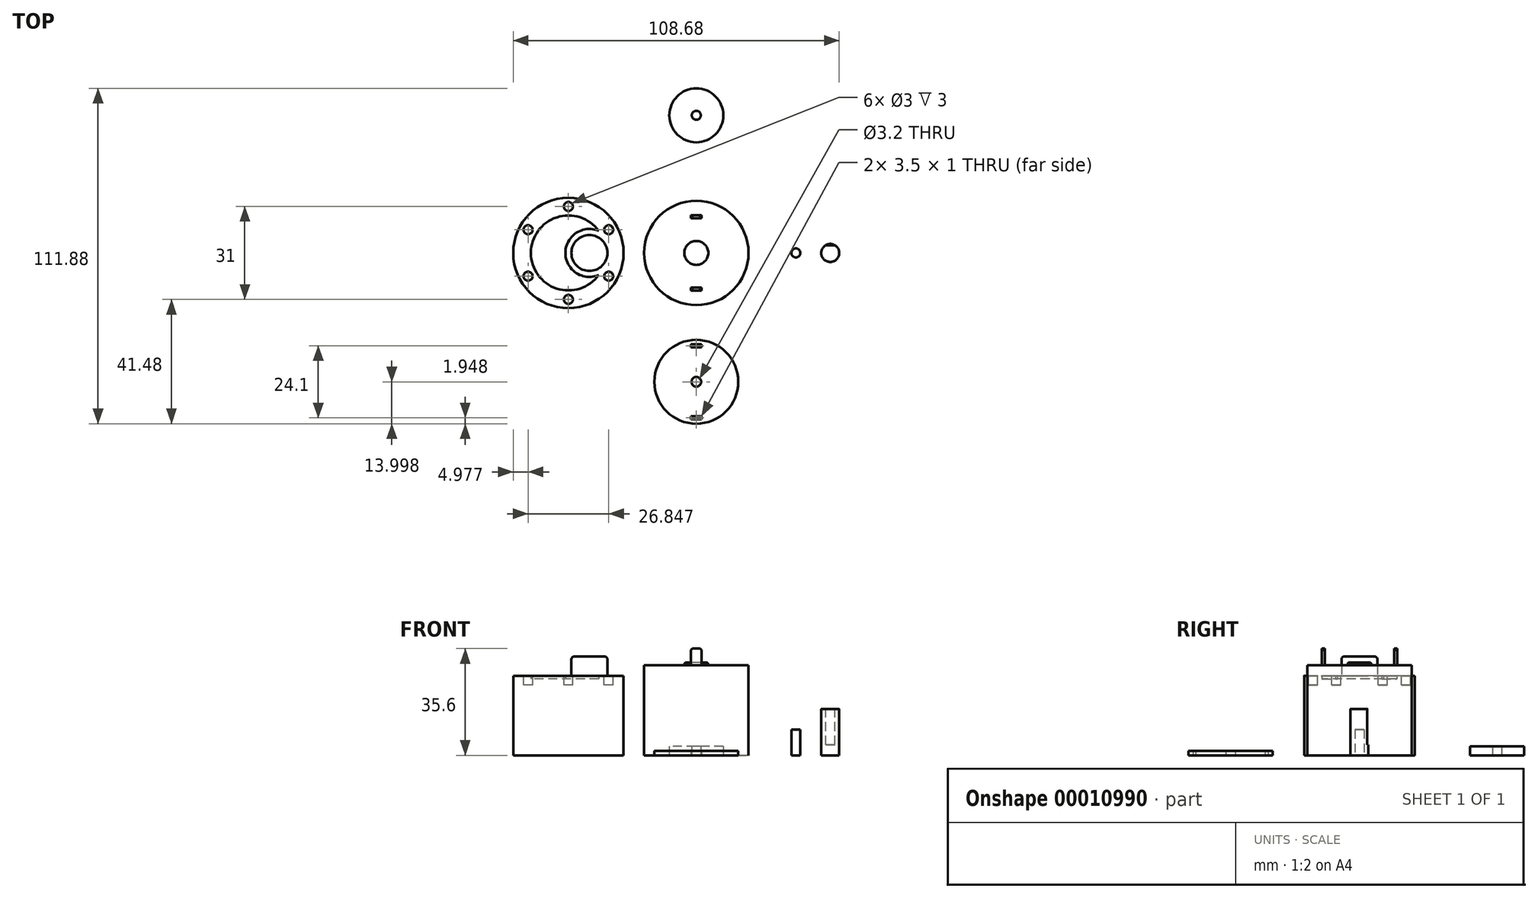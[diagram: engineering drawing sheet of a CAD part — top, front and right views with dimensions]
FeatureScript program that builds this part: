
annotation { "Feature Type Name" : "Feature", "Feature Type Description" : "" }
export const myFeature = defineFeature(function(context is Context, id is Id, definition is map)
    precondition{}
    {
        {
            var Q0;
            Q0=qCreatedBy(makeId("Top.planeOp"),FACE);
            var sketch = newSketch(context, id + "F0", { "sketchPlane" : qUnion([Q0])});
            skCircle(sketch, "E0", {"center": v(-42.64, 0) * mm, "radius": 18.4 * mm});
            skSolve(sketch);
        }
        {
            var Q0;
            Q0=makeQuery(id+"F0.imprint","IMPRINT",FACE,{"disambiguationData":[TD([[makeQuery(id+"F0.imprint","IMPRINT",EDGE,{"derivedFrom":sQuery(id+"F0.wireOp",EDGE,"E0")}),1.0]])]});
            extrude(context, id + "F1", {"entities" : qUnion([Q0]), "depth" : 25.5 * mm});
        }
        {
            var Q0;
            Q0=makeQuery(id+"F1.opExtrude","CAP_FACE",FACE,{"disambiguationData":[OSD([sQuery(id+"F0.wireOp",EDGE,"E0")])],"isStart":false});
            var sketch = newSketch(context, id + "F2", { "sketchPlane" : qUnion([Q0])});
            skArc(sketch, "E1", {"start": v(-32.55, 7.38) * mm, "mid": v(-55.14, 0) * mm, "end": v(-32.55, -7.38) * mm});
            skArc(sketch, "E2", {"start": v(-32.55, 7.38) * mm, "mid": v(-43.64, 0) * mm, "end": v(-32.55, -7.38) * mm});
            skSolve(sketch);
        }
        {
            var Q0;
            Q0=makeQuery(id+"F2.imprint","IMPRINT",FACE,{"disambiguationData":[TD([[makeQuery(id+"F2.imprint","IMPRINT",EDGE,{"derivedFrom":sQuery(id+"F2.wireOp",EDGE,"E1")}),-1.0]])]});
            extrude(context, id + "F3", {"entities" : qUnion([Q0]), "operationType" : NewBodyOperationType.ADD, "depth" : 1 * mm});
        }
        {
            var Q0;
            Q0=makeQuery(id+"F3.opExtrude","CAP_FACE",FACE,{"disambiguationData":[OSD([sQuery(id+"F0.wireOp",EDGE,"E0"),sQuery(id+"F2.wireOp",EDGE,"E1"),sQuery(id+"F2.wireOp",EDGE,"E2")])],"isStart":false});
            var sketch = newSketch(context, id + "F4", { "sketchPlane" : qUnion([Q0])});
            skCircle(sketch, "E3", {"center": v(-35.64, 0) * mm, "radius": 6 * mm});
            skSolve(sketch);
        }
        {
            var Q0;
            Q0=makeQuery(id+"F4.imprint","IMPRINT",FACE,{"disambiguationData":[TD([[makeQuery(id+"F4.imprint","IMPRINT",EDGE,{"derivedFrom":sQuery(id+"F4.wireOp",EDGE,"E3")}),1.0]])]});
            extrude(context, id + "F5", {"entities" : qUnion([Q0]), "operationType" : NewBodyOperationType.ADD, "depth" : 6.5 * mm});
        }
        {
            var Q0;
            Q0=makeQuery(id+"F5.opExtrude","CAP_EDGE",EDGE,{"disambiguationData":[OSD([sQuery(id+"F4.wireOp",EDGE,"E3")])],"isStart":false});
            fillet(context, id + "F6", {"entities" : qUnion([Q0]), "radius" : 1 * mm, "tangentPropagation" : true, "allowEdgeOverflow" : false});
        }
        {
            var Q0;
            Q0=makeQuery(id+"F3.opExtrude","CAP_FACE",FACE,{"disambiguationData":[OSD([sQuery(id+"F0.wireOp",EDGE,"E0"),sQuery(id+"F2.wireOp",EDGE,"E1"),sQuery(id+"F2.wireOp",EDGE,"E2")])],"isStart":false});
            var sketch = newSketch(context, id + "F7", { "sketchPlane" : qUnion([Q0])});
            skCircle(sketch, "E4", {"center": v(-42.64, 15.5) * mm, "radius": 1.5 * mm});
            skCircle(sketch, "E5.1.0", {"center": v(-56.06, 7.75) * mm, "radius": 1.5 * mm});
            skCircle(sketch, "E5.2.0", {"center": v(-56.06, -7.75) * mm, "radius": 1.5 * mm});
            skCircle(sketch, "E5.3.0", {"center": v(-42.64, -15.5) * mm, "radius": 1.5 * mm});
            skCircle(sketch, "E5.4.0", {"center": v(-29.22, -7.75) * mm, "radius": 1.5 * mm});
            skCircle(sketch, "E5.5.0", {"center": v(-29.22, 7.75) * mm, "radius": 1.5 * mm});
            skPoint(sketch, "E5.center", {"position": v(-42.64, 0) * mm});
            skSolve(sketch);
        }
        {
            var Q0;
            Q0 = qSketchRegion(id + "F7", true);
            extrude(context, id + "F8", {"entities" : qUnion([Q0]), "operationType" : NewBodyOperationType.REMOVE, "oppositeDirection" : true, "depth" : 3 * mm});
        }
        {
            var Q0;
            Q0=qCreatedBy(makeId("Top.planeOp"),FACE);
            var sketch = newSketch(context, id + "F9", { "sketchPlane" : qUnion([Q0])});
            skCircle(sketch, "E6", {"center": v(0, 0) * mm, "radius": 17.4 * mm});
            skSolve(sketch);
        }
        {
            var Q0;
            Q0=makeQuery(id+"F9.imprint","IMPRINT",FACE,{"disambiguationData":[TD([[makeQuery(id+"F9.imprint","IMPRINT",EDGE,{"derivedFrom":sQuery(id+"F9.wireOp",EDGE,"E6")}),1.0]])]});
            extrude(context, id + "F10", {"entities" : qUnion([Q0]), "depth" : 30 * mm});
        }
        {
            var Q0;
            Q0=makeQuery(id+"F10.opExtrude","CAP_FACE",FACE,{"disambiguationData":[OSD([sQuery(id+"F9.wireOp",EDGE,"E6")])],"isStart":false});
            var sketch = newSketch(context, id + "F11", { "sketchPlane" : qUnion([Q0])});
            skCircle(sketch, "E7", {"center": v(0, 0) * mm, "radius": 4 * mm});
            skSolve(sketch);
        }
        {
            var Q0;
            Q0=makeQuery(id+"F11.imprint","IMPRINT",FACE,{"disambiguationData":[TD([[makeQuery(id+"F11.imprint","IMPRINT",EDGE,{"derivedFrom":sQuery(id+"F11.wireOp",EDGE,"E7")}),1.0]])]});
            extrude(context, id + "F12", {"entities" : qUnion([Q0]), "operationType" : NewBodyOperationType.ADD, "depth" : 1 * mm});
        }
        {
            var Q0;
            Q0=makeQuery(id+"F12.opExtrude","CAP_EDGE",EDGE,{"disambiguationData":[OSD([sQuery(id+"F11.wireOp",EDGE,"E7")])],"isStart":false});
            fillet(context, id + "F13", {"entities" : qUnion([Q0]), "radius" : 0.7 * mm, "tangentPropagation" : true, "allowEdgeOverflow" : false});
        }
        {
            var Q0;
            Q0=makeQuery(id+"F10.opExtrude","CAP_FACE",FACE,{"disambiguationData":[OSD([sQuery(id+"F9.wireOp",EDGE,"E6")])],"isStart":false});
            var sketch = newSketch(context, id + "F14", { "sketchPlane" : qUnion([Q0])});
            skLineSegment(sketch, "E8.rect.bottom", {"start": v(1.75, 12.55) * mm, "end": v(-1.75, 12.55) * mm});
            skLineSegment(sketch, "E8.rect.top", {"start": v(1.75, 11.55) * mm, "end": v(-1.75, 11.55) * mm});
            skLineSegment(sketch, "E8.rect.left", {"start": v(1.75, 12.55) * mm, "end": v(1.75, 11.55) * mm});
            skLineSegment(sketch, "E8.rect.right", {"start": v(-1.75, 12.55) * mm, "end": v(-1.75, 11.55) * mm});
            skPoint(sketch, "E8.rect.middle", {"position": v(0, 12.05) * mm});
            skLineSegment(sketch, "E9.rect.bottom", {"start": v(1.75, -11.55) * mm, "end": v(-1.75, -11.55) * mm});
            skLineSegment(sketch, "E9.rect.top", {"start": v(1.75, -12.55) * mm, "end": v(-1.75, -12.55) * mm});
            skLineSegment(sketch, "E9.rect.left", {"start": v(1.75, -11.55) * mm, "end": v(1.75, -12.55) * mm});
            skLineSegment(sketch, "E9.rect.right", {"start": v(-1.75, -11.55) * mm, "end": v(-1.75, -12.55) * mm});
            skPoint(sketch, "E9.rect.middle", {"position": v(0, -12.05) * mm});
            skSolve(sketch);
        }
        {
            var Q0;
            Q0 = qSketchRegion(id + "F14", true);
            extrude(context, id + "F15", {"entities" : qUnion([Q0]), "operationType" : NewBodyOperationType.ADD, "depth" : 5.6 * mm});
        }
        {
            var Q0;
            Q0=makeQuery(id+"F15.opExtrude","CAP_EDGE",EDGE,{"disambiguationData":[OSD([sQuery(id+"F14.wireOp",EDGE,"E8.rect.left")])],"isStart":false});
            var Q1;
            Q1=makeQuery(id+"F15.opExtrude","CAP_EDGE",EDGE,{"disambiguationData":[OSD([sQuery(id+"F14.wireOp",EDGE,"E8.rect.right")])],"isStart":false});
            var Q2;
            Q2=makeQuery(id+"F15.opExtrude","CAP_EDGE",EDGE,{"disambiguationData":[OSD([sQuery(id+"F14.wireOp",EDGE,"E9.rect.left")])],"isStart":false});
            var Q3;
            Q3=makeQuery(id+"F15.opExtrude","CAP_EDGE",EDGE,{"disambiguationData":[OSD([sQuery(id+"F14.wireOp",EDGE,"E9.rect.right")])],"isStart":false});
            chamfer(context, id + "F16", {"entities" : qUnion([Q0, Q1, Q2, Q3]), "width" : 0.5 * mm, "tangentPropagation" : true});
        }
        {
            var Q0;
            Q0=qCreatedBy(makeId("Top.planeOp"),FACE);
            var sketch = newSketch(context, id + "F17", { "sketchPlane" : qUnion([Q0])});
            skCircle(sketch, "E10", {"center": v(33.18, 0) * mm, "radius": 1.5 * mm});
            skSolve(sketch);
        }
        {
            var Q0;
            Q0=makeQuery(id+"F17.imprint","IMPRINT",FACE,{"disambiguationData":[TD([[makeQuery(id+"F17.imprint","IMPRINT",EDGE,{"derivedFrom":sQuery(id+"F17.wireOp",EDGE,"E10")}),1.0]])]});
            extrude(context, id + "F18", {"entities" : qUnion([Q0]), "depth" : 8.55 * mm});
        }
        {
            var Q0;
            Q0=qCreatedBy(makeId("Top.planeOp"),FACE);
            var sketch = newSketch(context, id + "F19", { "sketchPlane" : qUnion([Q0])});
            skCircle(sketch, "E11", {"center": v(44.64, 0) * mm, "radius": 3 * mm});
            skSolve(sketch);
        }
        {
            var Q0;
            Q0=makeQuery(id+"F19.imprint","IMPRINT",FACE,{"disambiguationData":[TD([[makeQuery(id+"F19.imprint","IMPRINT",EDGE,{"derivedFrom":sQuery(id+"F19.wireOp",EDGE,"E11")}),1.0]])]});
            extrude(context, id + "F20", {"entities" : qUnion([Q0]), "depth" : 15.5 * mm});
        }
        {
            var Q0;
            Q0=makeQuery(id+"F20.opExtrude","CAP_FACE",FACE,{"disambiguationData":[OSD([sQuery(id+"F19.wireOp",EDGE,"E11")])],"isStart":false});
            var sketch = newSketch(context, id + "F21", { "sketchPlane" : qUnion([Q0])});
            skLineSegment(sketch, "E12", {"start": v(43.15, 2.6) * mm, "end": v(46.14, 2.6) * mm});
            skArc(sketch, "E13", {"start": v(46.14, 2.6) * mm, "mid": v(44.64, 3) * mm, "end": v(43.15, 2.6) * mm});
            skSolve(sketch);
        }
        {
            var Q0;
            Q0=makeQuery(id+"F20.opExtrude","CAP_EDGE",EDGE,{"disambiguationData":[OSD([sQuery(id+"F19.wireOp",EDGE,"E11")])],"isStart":false});
            fillet(context, id + "F22", {"entities" : qUnion([Q0]), "radius" : 0.2 * mm, "tangentPropagation" : true, "allowEdgeOverflow" : false});
        }
        {
            var Q0;
            Q0 = qSketchRegion(id + "F21", true);
            extrude(context, id + "F23", {"entities" : qUnion([Q0]), "operationType" : NewBodyOperationType.REMOVE, "oppositeDirection" : true, "depth" : 12 * mm});
        }
        {
            var Q0;
            Q0=qCreatedBy(makeId("Top.planeOp"),FACE);
            var sketch = newSketch(context, id + "F24", { "sketchPlane" : qUnion([Q0])});
            skCircle(sketch, "E14", {"center": v(0, 45.9) * mm, "radius": 9 * mm});
            skCircle(sketch, "E15", {"center": v(0, 45.9) * mm, "radius": 1.5 * mm});
            skSolve(sketch);
        }
        {
            var Q0;
            Q0 = qSketchRegion(id + "F24", true);
            extrude(context, id + "F25", {"entities" : qUnion([Q0]), "depth" : 3 * mm});
        }
        {
            var Q0;
            Q0=qCreatedBy(makeId("Top.planeOp"),FACE);
            var sketch = newSketch(context, id + "F26", { "sketchPlane" : qUnion([Q0])});
            skCircle(sketch, "E16", {"center": v(0, -42.98) * mm, "radius": 14 * mm});
            skPoint(sketch, "E17.rect.middle", {"position": v(0, -55.03) * mm});
            skPoint(sketch, "E18.rect.middle", {"position": v(0, -30.93) * mm});
            skLineSegment(sketch, "E18.rect.top", {"start": v(1.75, -31.43) * mm, "end": v(-1.75, -31.43) * mm});
            skLineSegment(sketch, "E18.rect.bottom", {"start": v(1.75, -30.43) * mm, "end": v(-1.75, -30.43) * mm});
            skLineSegment(sketch, "E17.rect.top", {"start": v(1.75, -55.53) * mm, "end": v(-1.75, -55.53) * mm});
            skLineSegment(sketch, "E17.rect.bottom", {"start": v(1.75, -54.53) * mm, "end": v(-1.75, -54.53) * mm});
            skLineSegment(sketch, "E18.rect.right", {"start": v(-1.75, -30.43) * mm, "end": v(-1.75, -31.43) * mm});
            skLineSegment(sketch, "E18.rect.left", {"start": v(1.75, -30.43) * mm, "end": v(1.75, -31.43) * mm});
            skLineSegment(sketch, "E17.rect.right", {"start": v(-1.75, -54.53) * mm, "end": v(-1.75, -55.53) * mm});
            skLineSegment(sketch, "E17.rect.left", {"start": v(1.75, -54.53) * mm, "end": v(1.75, -55.53) * mm});
            skCircle(sketch, "E19", {"center": v(0, -42.98) * mm, "radius": 1.6 * mm});
            skSolve(sketch);
        }
        {
            var Q0;
            Q0=makeQuery(id+"F26.imprint","IMPRINT",FACE,{"disambiguationData":[TD([[makeQuery(id+"F26.imprint","IMPRINT",EDGE,{"derivedFrom":sQuery(id+"F26.wireOp",EDGE,"E16")}),1.0]])]});
            extrude(context, id + "F27", {"entities" : qUnion([Q0]), "depth" : 1.5 * mm});
        }
    });
